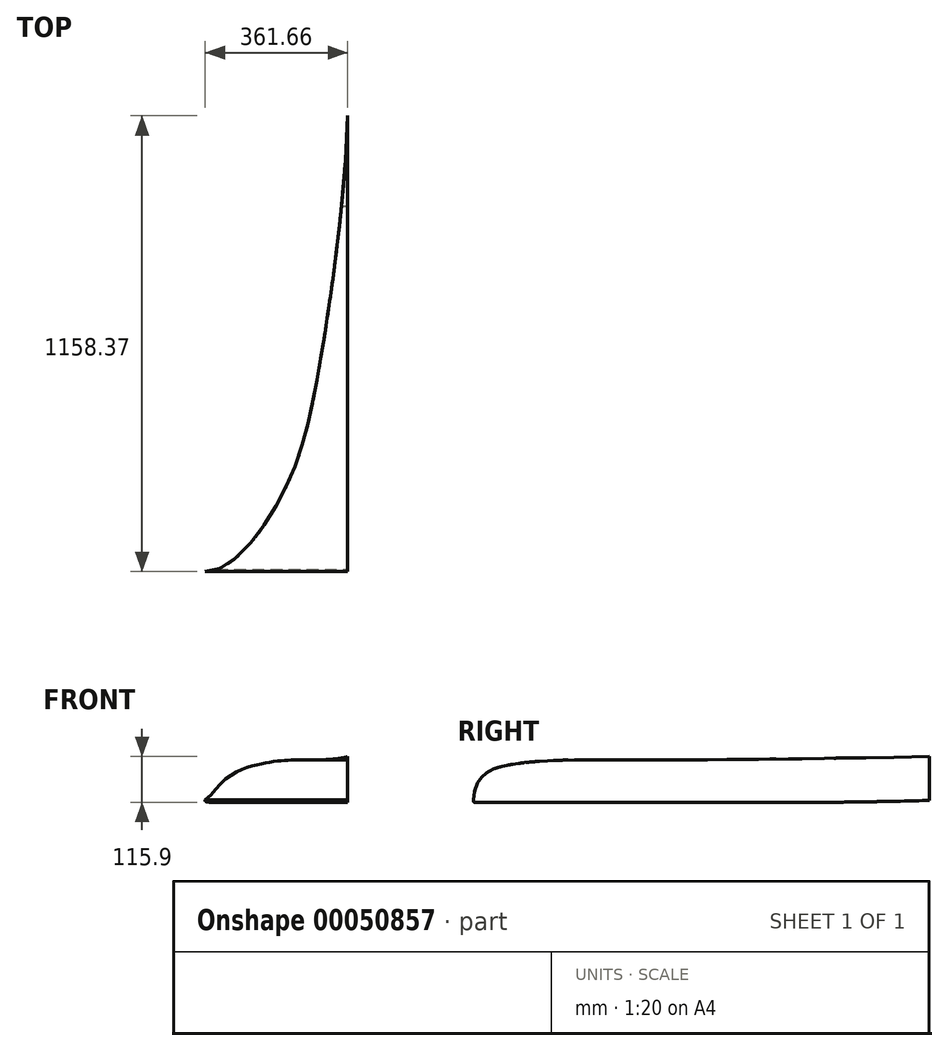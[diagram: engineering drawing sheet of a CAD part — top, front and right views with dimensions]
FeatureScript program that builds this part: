
annotation { "Feature Type Name" : "Feature", "Feature Type Description" : "" }
export const myFeature = defineFeature(function(context is Context, id is Id, definition is map)
    precondition{}
    {
        {
            var Q0;
            Q0=qCreatedBy(makeId("Top.planeOp"),FACE);
            var sketch = newSketch(context, id + "F0", { "sketchPlane" : qUnion([Q0])});
            skLineSegment(sketch, "E0.rect.bottom", {"start": v(365, 1225) * mm, "end": v(-365, 1225) * mm});
            skLineSegment(sketch, "E0.rect.top", {"start": v(365, -1225) * mm, "end": v(-365, -1225) * mm});
            skLineSegment(sketch, "E0.rect.left", {"start": v(365, 1225) * mm, "end": v(365, -1225) * mm});
            skLineSegment(sketch, "E0.rect.right", {"start": v(-365, 1225) * mm, "end": v(-365, -1225) * mm});
            skPoint(sketch, "E1.positionSnap0", {"position": v(0, 0) * mm});
            skPoint(sketch, "E2", {"position": v(365, 0) * mm});
            skPoint(sketch, "E3", {"position": v(0, 1225) * mm});
            skFitSpline(sketch, "E4", {"points": [v(0, 1225) * mm, v(55.86, 1215.11) * mm, v(128.28, 1155.33) * mm, v(256.28, 920.4) * mm, v(337.12, 581.06) * mm, v(365, 194.76) * mm, v(354.82, -239.14) * mm, v(284.5, -752.76) * mm, v(221.27, -982.07) * mm, v(111.27, -1160.75) * mm, v(36.86, -1218) * mm, v(0, -1225) * mm], "startDerivative": vector(1197.88, -85.16) * mm, "endDerivative": vector(-883.88, 14.55) * mm});
            skFitSpline(sketch, "E5.MirrorCS", {"points": [v(0, 1225) * mm, v(-55.86, 1215.11) * mm, v(-128.28, 1155.33) * mm, v(-256.28, 920.4) * mm, v(-337.12, 581.06) * mm, v(-365, 194.76) * mm, v(-354.82, -239.14) * mm, v(-284.5, -752.76) * mm, v(-221.27, -982.07) * mm, v(-111.27, -1160.75) * mm, v(-36.86, -1218) * mm, v(0, -1225) * mm], "startDerivative": vector(-1197.88, -85.16) * mm, "endDerivative": vector(883.88, 14.55) * mm});
            skSolve(sketch);
        }
        {
            var Q0;
            {var subQ4=sQuery(id+"F0.wireOp",EDGE,"E4");var subQ8=sQuery(id+"F0.wireOp",EDGE,"E0.rect.left");var subQ9=makeQuery(id+"F0.imprint","INTERSECT",VERTEX,{"disambiguationData":[OD(0.0)],"derivedFrom":[subQ8,subQ4]});Q0=makeQuery(id+"F0.imprint","IMPRINT",FACE,{"disambiguationData":[TD([[makeQuery(id+"F0.imprint","IMPRINT",EDGE,{"disambiguationData":[TD([[subQ9,-1.0]])],"derivedFrom":subQ8}),-1.0]])]});}
            var Q1;
            Q1=sQuery(id+"F0.wireOp",EDGE,"E4");
            var Q2;
            Q2=sQuery(id+"F0.wireOp",EDGE,"E5.MirrorCS");
            extrude(context, id + "F1", {"entities" : qUnion([Q0]), "surfaceEntities" : qUnion([Q1, Q2]), "depth" : 254 * mm});
        }
        {
            var Q0;
            Q0=qCreatedBy(makeId("Right.planeOp"),FACE);
            var sketch = newSketch(context, id + "F2", { "sketchPlane" : qUnion([Q0])});
            skFitSpline(sketch, "E6", {"points": [v(-1224.1, 0) * mm, v(-1224.98, 1.84) * mm, v(-1218.5, 40.32) * mm, v(-1203.53, 64.2) * mm, v(-1180.7, 81.26) * mm, v(-1135.99, 94.48) * mm, v(-1028.6, 105.72) * mm, v(-767.24, 107.38) * mm, v(-213, 113.38) * mm, v(458.13, 131.8) * mm, v(888.91, 164.54) * mm, v(1064.6, 190.16) * mm, v(1160.7, 212.85) * mm, v(1211.05, 217.24) * mm, v(1216.65, 204.16) * mm, v(1143.99, 169.25) * mm, v(969.67, 120.15) * mm, v(590.71, 44.04) * mm, v(239.98, 16.7) * mm, v(-296.88, 0) * mm, v(-1142.23, 0) * mm, v(-1184.17, 0) * mm, v(-1220.12, 0) * mm, v(-1224.1, 0) * mm]});
            skLineSegment(sketch, "E7.bottom", {"start": v(-1256.04, 300) * mm, "end": v(1292.54, 300) * mm});
            skLineSegment(sketch, "E7.top", {"start": v(-1256.04, -74.25) * mm, "end": v(1292.54, -74.25) * mm});
            skLineSegment(sketch, "E7.left", {"start": v(-1256.04, 300) * mm, "end": v(-1256.04, -74.25) * mm});
            skLineSegment(sketch, "E7.right", {"start": v(1292.54, 300) * mm, "end": v(1292.54, -74.25) * mm});
            skSolve(sketch);
        }
        {
            var Q0;
            Q0=makeQuery(id+"F2.imprint","IMPRINT",FACE,{"disambiguationData":[TD([[makeQuery(id+"F2.imprint","IMPRINT",EDGE,{"derivedFrom":sQuery(id+"F2.wireOp",EDGE,"E6")}),1.0]])]});
            var Q1;
            Q1=sQuery(id+"F2.wireOp",EDGE,"E6");
            var Q2;
            Q2=sQuery(id+"F2.wireOp",EDGE,"E7.top");
            var Q3;
            Q3=sQuery(id+"F2.wireOp",EDGE,"E7.left");
            var Q4;
            Q4=sQuery(id+"F2.wireOp",EDGE,"E7.bottom");
            var Q5;
            Q5=sQuery(id+"F2.wireOp",EDGE,"E7.right");
            extrude(context, id + "F3", {"entities" : qUnion([Q0]), "operationType" : NewBodyOperationType.REMOVE, "surfaceEntities" : qUnion([Q1, Q2, Q3, Q4, Q5]), "endBound" : BoundingType.THROUGH_ALL, "oppositeDirection" : true, "depth" : 25.4 * mm, "hasSecondDirection" : true, "secondDirectionBound" : SecondDirectionBoundingType.THROUGH_ALL, "secondDirectionOppositeDirection" : false, "secondDirectionDepth" : 25.4 * mm});
        }
    });
